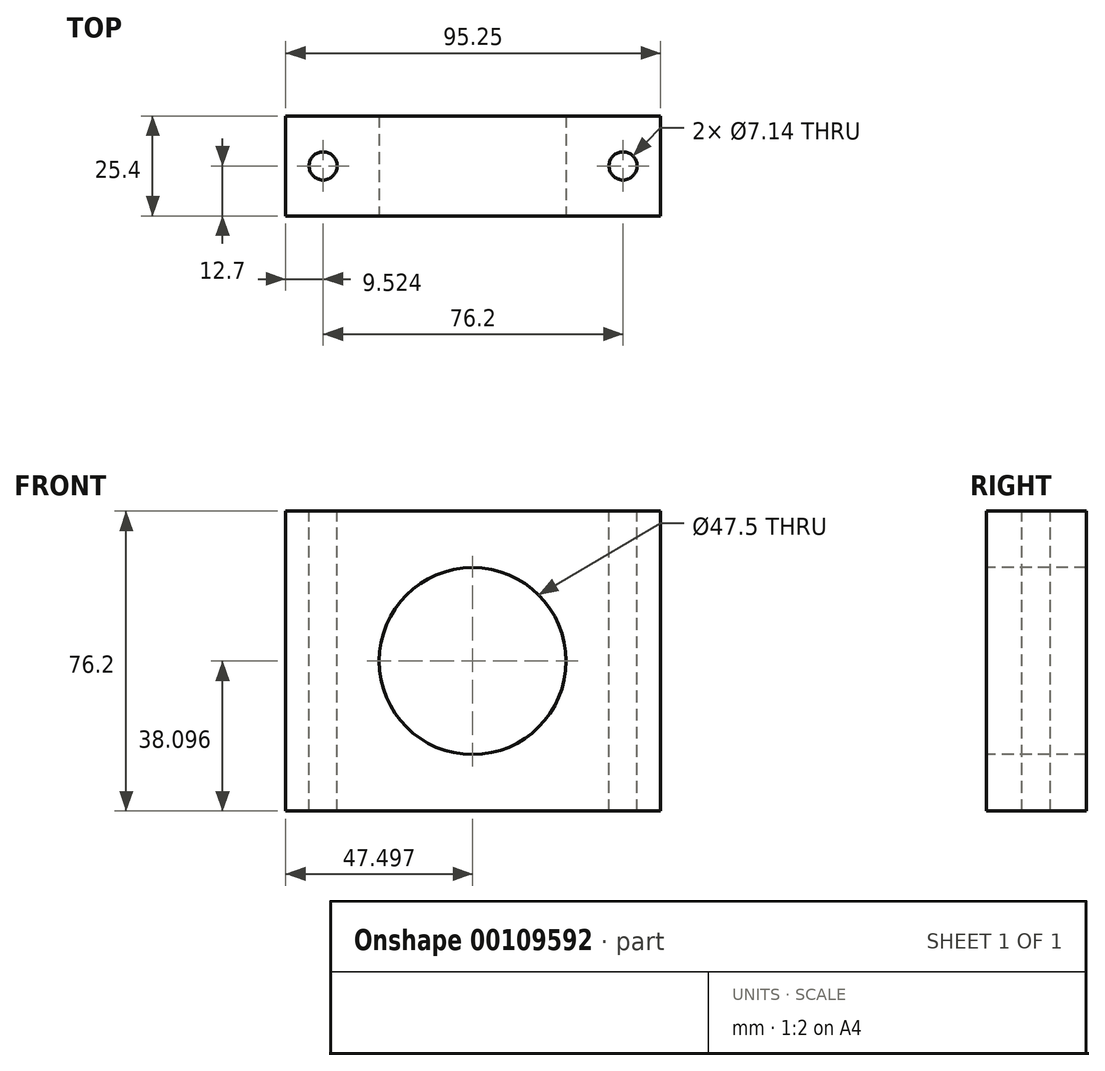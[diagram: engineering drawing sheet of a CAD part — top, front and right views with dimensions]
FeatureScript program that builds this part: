
annotation { "Feature Type Name" : "Feature", "Feature Type Description" : "" }
export const myFeature = defineFeature(function(context is Context, id is Id, definition is map)
    precondition{}
    {
        {
            var Q0;
            Q0=qCreatedBy(makeId("Front.planeOp"),FACE);
            var sketch = newSketch(context, id + "F0", { "sketchPlane" : qUnion([Q0])});
            skLineSegment(sketch, "E0.bottom", {"start": v(-32.22, 33.08) * mm, "end": v(63.03, 33.08) * mm});
            skLineSegment(sketch, "E0.top", {"start": v(-32.22, -43.12) * mm, "end": v(63.03, -43.12) * mm});
            skLineSegment(sketch, "E0.left", {"start": v(-32.22, 33.08) * mm, "end": v(-32.22, -43.12) * mm});
            skLineSegment(sketch, "E0.right", {"start": v(63.03, 33.08) * mm, "end": v(63.03, -43.12) * mm});
            skSolve(sketch);
        }
        {
            var Q0;
            Q0 = qSketchRegion(id + "F0", true);
            extrude(context, id + "F1", {"entities" : qUnion([Q0]), "depth" : 25.4 * mm});
        }
        {
            var Q0;
            Q0=makeQuery(id+"F1.opExtrude","CAP_FACE",FACE,{"disambiguationData":[OSD([sQuery(id+"F0.wireOp",EDGE,"E0.bottom"),sQuery(id+"F0.wireOp",EDGE,"E0.top"),sQuery(id+"F0.wireOp",EDGE,"E0.left"),sQuery(id+"F0.wireOp",EDGE,"E0.right")])],"isStart":false});
            var sketch = newSketch(context, id + "F2", { "sketchPlane" : qUnion([Q0])});
            skCircle(sketch, "E1", {"center": v(15.28, -5.02) * mm, "radius": 23.75 * mm});
            skLineSegment(sketch, "E2", {"start": v(-32.22, -5.02) * mm, "end": v(63.03, -5.02) * mm, "construction": true});
            skSolve(sketch);
        }
        {
            var Q0;
            Q0 = qSketchRegion(id + "F2", true);
            var Q1;
            Q1=makeQuery(id+"F1.opExtrude","CAP_FACE",FACE,{"disambiguationData":[OSD([sQuery(id+"F0.wireOp",EDGE,"E0.bottom"),sQuery(id+"F0.wireOp",EDGE,"E0.top"),sQuery(id+"F0.wireOp",EDGE,"E0.left"),sQuery(id+"F0.wireOp",EDGE,"E0.right")])],"isStart":true});
            extrude(context, id + "F3", {"entities" : qUnion([Q0]), "operationType" : NewBodyOperationType.REMOVE, "endBound" : BoundingType.UP_TO_SURFACE, "oppositeDirection" : true, "endBoundEntityFace" : qUnion([Q1]), "depth" : 25.4 * mm});
        }
        {
            var Q0;
            Q0=makeQuery(id+"F1.opExtrude","SWEPT_FACE",FACE,{"disambiguationData":[OSD([sQuery(id+"F0.wireOp",EDGE,"E0.bottom")])]});
            var sketch = newSketch(context, id + "F4", { "sketchPlane" : qUnion([Q0])});
            skCircle(sketch, "E3", {"center": v(-22.7, -12.7) * mm, "radius": 3.57 * mm});
            skCircle(sketch, "E4", {"center": v(53.5, -12.7) * mm, "radius": 3.57 * mm});
            skSolve(sketch);
        }
        {
            var Q0;
            Q0=makeQuery(id+"F4.imprint","IMPRINT",FACE,{"disambiguationData":[TD([[makeQuery(id+"F4.imprint","IMPRINT",EDGE,{"derivedFrom":sQuery(id+"F4.wireOp",EDGE,"E3")}),1.0]])]});
            var Q1;
            Q1=makeQuery(id+"F4.imprint","IMPRINT",FACE,{"disambiguationData":[TD([[makeQuery(id+"F4.imprint","IMPRINT",EDGE,{"derivedFrom":sQuery(id+"F4.wireOp",EDGE,"E4")}),1.0]])]});
            var Q2;
            Q2=makeQuery(id+"F1.opExtrude","SWEPT_FACE",FACE,{"disambiguationData":[OSD([sQuery(id+"F0.wireOp",EDGE,"E0.top")])]});
            extrude(context, id + "F5", {"entities" : qUnion([Q0, Q1]), "operationType" : NewBodyOperationType.REMOVE, "endBound" : BoundingType.UP_TO_SURFACE, "oppositeDirection" : true, "endBoundEntityFace" : qUnion([Q2]), "depth" : 25.4 * mm});
        }
    });
